annotation { "Feature Type Name" : "Feature", "Feature Type Description" : "" }
export const myFeature = defineFeature(function(context is Context, id is Id, definition is map)
    precondition{}
    {
        {
            var Q0;
            Q0=qCreatedBy(makeId("Front.planeOp"),FACE);
            var sketch = newSketch(context, id + "F0", { "sketchPlane" : qUnion([Q0])});
            skLineSegment(sketch, "E0", {"start": v(-39.43, -292) * mm, "end": v(-39.43, 317.6) * mm});
            skLineSegment(sketch, "E1", {"start": v(-39.43, -292) * mm, "end": v(265.37, -292) * mm});
            skLineSegment(sketch, "E2", {"start": v(265.37, -292) * mm, "end": v(265.37, 317.6) * mm});
            skArc(sketch, "E3", {"start": v(265.37, 317.6) * mm, "mid": v(112.97, 437) * mm, "end": v(-39.43, 317.6) * mm});
            skText(sketch, "E4", { "text": "Davey Jones\nLocker\n1800 - 1900", "fontName": "OpenSans-Regular.ttf"});
            const initialGuessF0  = {"E4": [-0.03943, -0.02154, 1, 0, 0.03882]};
            skSetInitialGuess(sketch, initialGuessF0);
            skSolve(sketch);
        }
        {
            var Q0;
            Q0 = qSketchRegion(id + "F0", true);
            extrude(context, id + "F1", {"entities" : qUnion([Q0]), "depth" : 127 * mm});
        }
    });